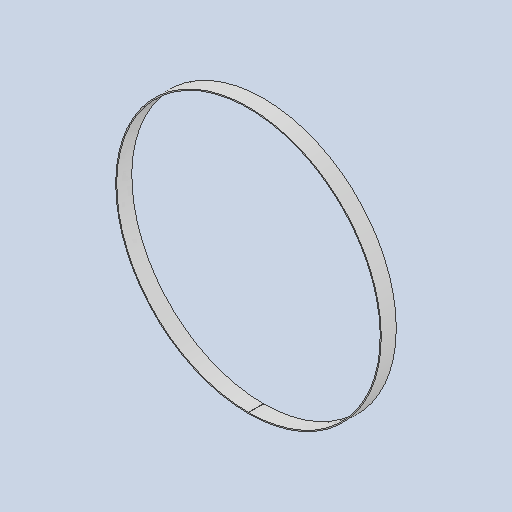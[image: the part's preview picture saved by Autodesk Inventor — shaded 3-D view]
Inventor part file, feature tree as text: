
AUTODESK INVENTOR PART (.ipt)
format: ipt  version: 2025 (Build 290162010, 162A)  size: 188,928 bytes
history: native  units: mm
features: sheet_metal_op x3, other x2, sketch x1
ambient origin geometry x8: Origin, YZ Plane, XZ Plane, XY Plane, X Axis, Y Axis, Z Axis, Center Point
bodies: Body1 (feature_tree)
feature tree (6):
  sheet_metal_op  "Contour Flange1"
  sketch  "Sketch1"  dims[d28=508.0mm d30=62.8144mm d31=2.0mm d32=2.0mm d33=1.0mm d34=4.0mm d35=2.0mm d36=29.0mm d37=2.0mm d38=2.0mm d39=8.0mm d40=2.0mm d41=2.0mm]
  other  "Plate2"
  sheet_metal_op  "Bend1"
  sheet_metal_op  "Corner1"
  other  "Definition1"
